# Revit family: Protek
name_source: partatom
category: Luminarias
revit_build: Autodesk Revit 2015 (Build: 20140606_1530(x64)
units: mm (PartAtom-declared; Revit-internal decimal feet)

## types (4) — shared parameters
Anchura rectángulo de emisión = 67 mm
Cambio de temperatura de color de luz atenuada = <Ninguno>
Fabricante = SECOM ILUMINACIÓN
Filtro de color = 16777215
Forma visible en renderización = No
Longitud de rectángulo de emisión = 140 mm  [stored 0.459318 ft]
Lámpara = LED Osram Duris E5
Modelo = Protek
Ángulo de inclinación = 90.00°

## per-type parameters (varying)
| type | Archivo de red fotométrica | Comentarios de vataje | Descripción |
| Protek 8 W | 4125 01 08 84.IES | 8W | 4125 01 08 84 |
| Protek 16 W | 4125 01 16 84.IES | 16 W | 4125 01 16 84 |
| Protek 25 W | 4125 01 25 84.IES | 25 W | 4125 01 25 84 |
| Protek 50 W | 4125 01 50 84.IES | 50 W | 4125 01 50 84 |

note: [stored X ft] marks values corroborated as IEEE doubles in the binary element streams (Revit-internal decimal feet)
